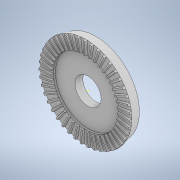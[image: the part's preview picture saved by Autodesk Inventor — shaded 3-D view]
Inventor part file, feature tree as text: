
AUTODESK INVENTOR PART (.ipt)
format: ipt  version: 2021 (Build 250183000, 183)  size: 599,040 bytes
history: native  units: in
note: dims shown in document units (in); Inventor stores cm internally (conversion verified against a paired STEP export)
features: sketch x4, extrude x2, revolve x1, draft x1
ambient origin geometry x8: Origin, YZ Plane, XZ Plane, XY Plane, X Axis, Y Axis, Z Axis, Center Point
bodies: Solid1 (feature_tree)
feature tree (8):
  sketch  "Sketch1"  dims[d0=0.4724in d1=1.5748in]
  revolve  "Revolution1"  [1 undecoded]
  extrude  "Extrusion1"  Depth=2.7559in
  extrude  "Extrusion2"  Depth=3.937in
  draft  "FaceDraft1"
  sketch  "Sketch2"  dims[d2=2.7559in d3=0.0861in]
  sketch  "Sketch3"  dims[d4=90.0deg d5=3.937in]
  sketch  "Sketch4"  dims[d6=5.5118in d7=0.1181in d8=0.0in d9=5.5118in d10=0.1575in d11=0.0787in d12=0.1181in d13=0.0591in d14=16.9291in d16=360.0deg d18=0.1181in d19=-0.0861in d20=-0.0862in]
note: 1 required parameter value undecoded (feature->parameter linkage not recoverable at this tier; creation-order binding heuristic only, values carry confidence <= 0.55)
